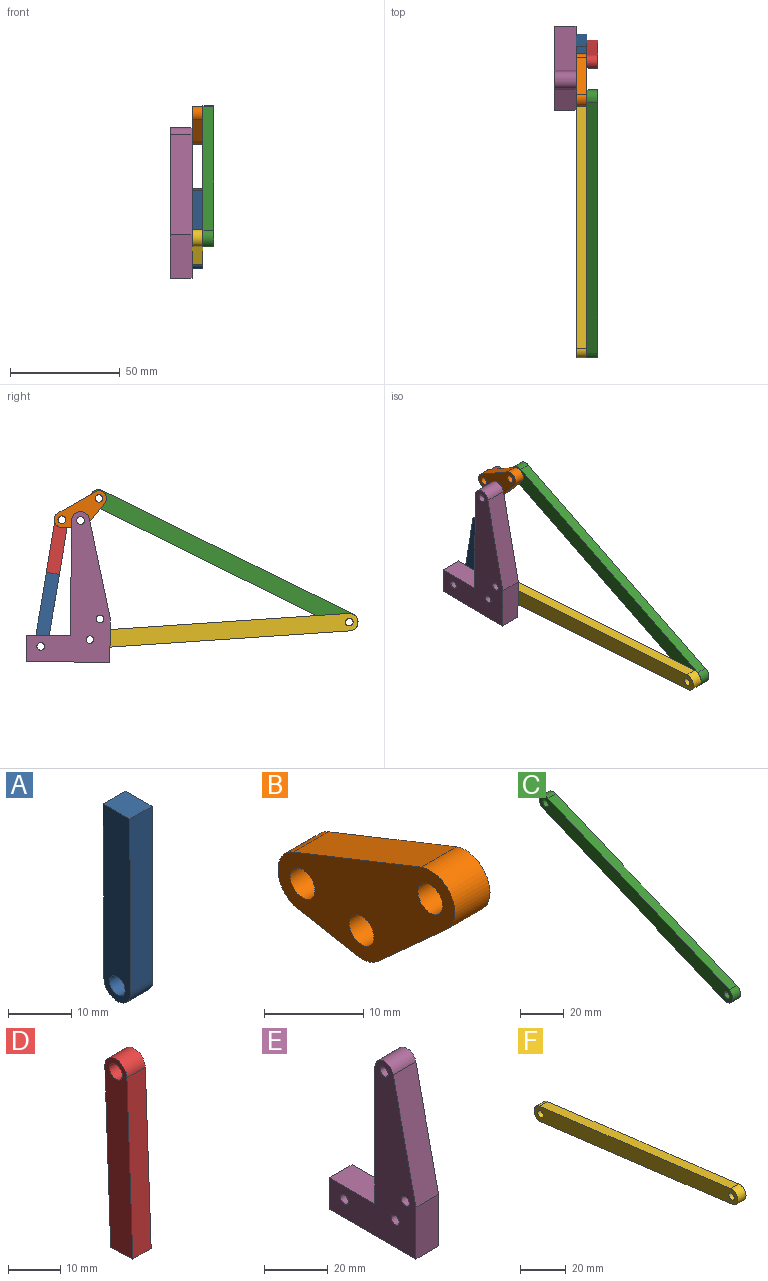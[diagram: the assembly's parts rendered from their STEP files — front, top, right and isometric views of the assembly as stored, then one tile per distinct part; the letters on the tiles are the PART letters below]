
ASSEMBLY  parts=6 mates=8
PART A: 7 faces, bbox 5x6.2x36.8 mm
  f0: cylinder r=3mm len=6mm, axis (1,0,0), area 47.1mm2, adj f1,f3,f5,f6
  f1: plane 33.78x5mm, normal (0,1,-0.01), area 168.9mm2, adj f0,f2,f5,f6
  f2: plane 6x5mm, normal (0,0.01,1), area 30mm2, adj f1,f3,f5,f6
  f3: plane 33.78x5mm, normal (0,-1,0.01), area 168.9mm2, adj f0,f2,f5,f6
  f4: cylinder r=1.75mm len=5mm, axis (1,0,0), area 55mm2, adj f5,f6
  f5: plane 36.8x6.19mm, normal (1,0,0), area 207.2mm2, adj f0,f1,f2,f3,f4
  f6: plane 36.8x6.19mm, normal (-1,0,0), area 207.2mm2, adj f0,f1,f2,f3,f4
PART B: 11 faces, bbox 5x25.2x15.8 mm
  f0: plane 18.16x7.22mm, normal (0,0.37,0.93), area 97.7mm2, adj f1,f8,f9,f10
  f1: cylinder r=3.5mm len=6.1mm, axis (1,0,0), area 48.8mm2, adj f0,f2,f9,f10
  f2: plane 9.76x8.79mm, normal (0,-0.67,-0.74), area 65.7mm2, adj f1,f3,f9,f10
  f3: cylinder r=3.5mm len=5mm, axis (1,0,0), area 16.1mm2, adj f2,f4,f9,f10
  f4: plane 8.4x5mm, normal (0,0.18,-0.98), area 42.7mm2, adj f3,f8,f9,f10
  f5: cylinder r=1.75mm len=5mm, axis (1,0,0), area 55mm2, adj f9,f10
  f6: cylinder r=1.75mm len=5mm, axis (1,0,0), area 55mm2, adj f9,f10
  f7: cylinder r=1.75mm len=5mm, axis (1,0,0), area 55mm2, adj f9,f10
  f8: cylinder r=3.5mm len=6.69mm, axis (1,0,0), area 45.1mm2, adj f0,f4,f9,f10
  f9: plane 25.16x15.79mm, normal (1,0,0), area 198.6mm2, adj f0,f1,f2,f3,f4,f5,f6,f7
  f10: plane 25.16x15.79mm, normal (-1,0,0), area 198.6mm2, adj f0,f1,f2,f3,f4,f5,f6,f7
PART C: 8 faces, bbox 5x125.7x57 mm
  f0: plane 117.7x48.98mm, normal (0,0.38,-0.92), area 637.4mm2, adj f1,f5,f6,f7
  f1: cylinder r=4mm len=7.69mm, axis (1,0,0), area 62.8mm2, adj f0,f2,f6,f7
  f2: plane 117.7x48.98mm, normal (0,-0.38,0.92), area 637.4mm2, adj f1,f5,f6,f7
  f3: cylinder r=1.75mm len=5mm, axis (1,0,0), area 55mm2, adj f6,f7
  f4: cylinder r=1.75mm len=5mm, axis (1,0,0), area 55mm2, adj f6,f7
  f5: cylinder r=4mm len=7.69mm, axis (1,0,0), area 62.8mm2, adj f0,f2,f6,f7
  f6: plane 125.7x56.98mm, normal (1,0,0), area 1050.9mm2, adj f0,f1,f2,f3,f4,f5
  f7: plane 125.7x56.98mm, normal (-1,0,0), area 1050.9mm2, adj f0,f1,f2,f3,f4,f5
PART D: 7 faces, bbox 5x7.6x45 mm
  f0: plane 6x5mm, normal (0,-0.04,-1), area 30mm2, adj f1,f4,f5,f6
  f1: plane 41.88x5mm, normal (0,1,-0.04), area 209.5mm2, adj f0,f2,f5,f6
  f2: cylinder r=3mm len=6mm, axis (1,0,0), area 47.1mm2, adj f1,f4,f5,f6
  f3: cylinder r=1.75mm len=5mm, axis (1,0,0), area 55mm2, adj f5,f6
  f4: plane 41.88x5mm, normal (0,-1,0.04), area 209.5mm2, adj f0,f2,f5,f6
  f5: plane 44.99x7.59mm, normal (1,0,0), area 256mm2, adj f0,f1,f2,f3,f4
  f6: plane 44.99x7.59mm, normal (-1,0,0), area 256mm2, adj f0,f1,f2,f3,f4
PART E: 13 faces, bbox 10x38.3x68.7 mm
  f0: plane 11.98x10mm, normal (0,1,0), area 119.8mm2, adj f1,f10,f11,f12
  f1: plane 38.27x10mm, normal (0,0,-1), area 382.7mm2, adj f0,f2,f11,f12
  f2: plane 19.81x10mm, normal (0,-1,0), area 198.1mm2, adj f1,f3,f11,f12
  f3: plane 45.69x10.06mm, normal (0,-0.98,0.22), area 467.8mm2, adj f2,f4,f11,f12
  f4: cylinder r=4.08mm len=10mm, axis (-1,0,0), area 119.4mm2, adj f3,f5,f11,f12
  f5: plane 52.64x10mm, normal (0,1,0), area 526.4mm2, adj f4,f10,f11,f12
  f6: cylinder r=1.75mm len=10mm, axis (-1,0,0), area 110mm2, adj f11,f12
  f7: cylinder r=1.75mm len=10mm, axis (-1,0,0), area 110mm2, adj f11,f12
  f8: cylinder r=1.75mm len=10mm, axis (-1,0,0), area 110mm2, adj f11,f12
  f9: cylinder r=1.75mm len=10mm, axis (-1,0,0), area 110mm2, adj f11,f12
  f10: plane 20.15x10mm, normal (0,0,1), area 201.5mm2, adj f0,f5,f11,f12
  f11: plane 68.7x38.27mm, normal (-1,0,0), area 1179.4mm2, adj f0,f1,f2,f3,f4,f5,f6,f7
  f12: plane 68.7x38.27mm, normal (1,0,0), area 1179.4mm2, adj f0,f1,f2,f3,f4,f5,f6,f7
PART F: 8 faces, bbox 5x125.7x22.9 mm
  f0: plane 117.72x14.88mm, normal (0,-0.13,-0.99), area 593.3mm2, adj f1,f5,f6,f7
  f1: cylinder r=4mm len=7.97mm, axis (1,0,0), area 62.8mm2, adj f0,f2,f6,f7
  f2: plane 117.72x14.88mm, normal (0,0.13,0.99), area 593.3mm2, adj f1,f5,f6,f7
  f3: cylinder r=1.75mm len=5mm, axis (1,0,0), area 55mm2, adj f6,f7
  f4: cylinder r=1.75mm len=5mm, axis (1,0,0), area 55mm2, adj f6,f7
  f5: cylinder r=4mm len=7.97mm, axis (1,0,0), area 62.8mm2, adj f0,f2,f6,f7
  f6: plane 125.72x22.88mm, normal (1,0,0), area 980.3mm2, adj f0,f1,f2,f3,f4,f5
  f7: plane 125.72x22.88mm, normal (-1,0,0), area 980.3mm2, adj f0,f1,f2,f3,f4,f5
PLACE A rot(axis=(1,0,0),9.8deg) t=(2.62,-12.11,-21.04)mm
PLACE B rot(axis=(-1,0,0),8.2deg) t=(2.62,-20.64,-13.39)mm
PLACE C rot(axis=(1,0,0),3.7deg) t=(2.62,-9.48,-15.16)mm
PLACE D rot(axis=(1,0,0),11.6deg) t=(2.62,-4.3,-21.39)mm
PLACE E rot(axis=(1,0,0),0.6deg) t=(2.62,-10.5,-16.02)mm fixed
PLACE F rot(axis=(1,0,0),3.3deg) t=(2.62,-9.47,-15.9)mm
MATE planar A.f1 <-> D.f1  axis (0,0.99,0.16) through (0.12,20.18,-11.39)mm
MATE revolute D.f2 <-> B.f5  axis (-1,0,0) through (2.62,10.37,29.27)mm
MATE planar A.f1 <-> D.f1  axis (0,0.99,0.16) through (0.12,20.18,-11.39)mm
MATE revolute C.f1 <-> B.f1  axis (-1,0,0) through (2.62,-6.57,39.02)mm
MATE revolute B.f3 <-> E.f4  axis (-1,0,0) through (-2.38,1.83,28.92)mm
MATE revolute E.f7 <-> F.f1  axis (1,0,0) through (-2.38,-2.46,-25.49)mm
MATE revolute F.f3 <-> C.f3  axis (1,0,0) through (2.62,-120.85,-17.48)mm
MATE revolute A.f0 <-> E.f9  axis (1,0,0) through (-2.38,19.99,-28.54)mm
